# Revit family: WINMASTER_VANDRET_BUNDSAMLING
name_source: partatom
category: Detail Items
units: mm (PartAtom-declared; Revit-internal decimal feet)

## family parameters
Rotate with component = No
Section Shape = Not Defined
Shared = No

## types (1)
- WINMASTER_VANDRET_BUNDSAMLING
    Anvendelse = Understøtter vinduet i forbindelse med montage
    Bæreevne af Isoleringsbjælke = Punktbelastning 100 kg
    Description = Vandret Bundsamling m. Isoleringsbjælke
    Funktion = Stabilisere pladefalsen ud mod formuren ved vinduer og dørhuller
    Isoleringsbjælke (mål) = 50 x Justerbar i højden mm
    Linjetab af Isoleringsbjælke = 0,033 W/mK
    Linjetab af pladefalsen = 0,33 W/mK
    Manufacturer = WINMASTER
    Material_Harpun Klods = Plast
    Material_Isolering = PU Skum
    Material_Isoleringsbjælke = Trykfast polystyren
    Material_Mørterl = Limmørtel
    Material_Pladefalsen = Lysningsplade
    URL = https://winmaster.dk
    Udført af = Tegnestuen Tankestregen
    WINMASTER_Bærebjælke = https://winmaster.dk
    WINMASTER_Isoleringsbjælke = https://winmaster.dk
    WINMASTER_Pladefalse = https://winmaster.dk
    WINMASTER_URL = https://winmaster.dk

## geometry (parser evidence)
native form markers: Sweep x7
no freeform markers — native parametric forms only
